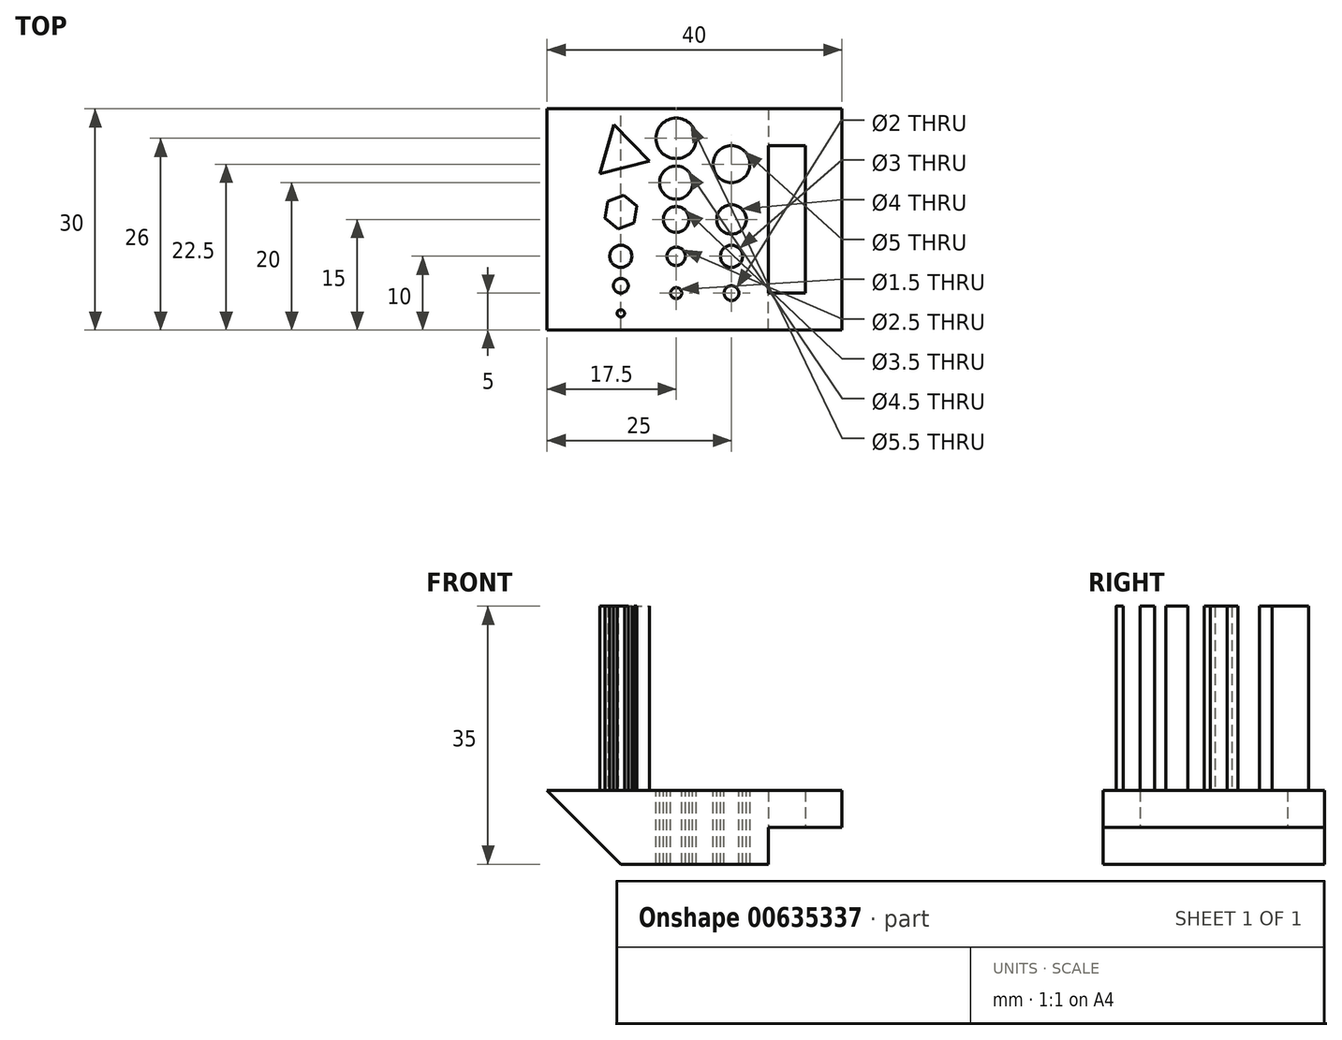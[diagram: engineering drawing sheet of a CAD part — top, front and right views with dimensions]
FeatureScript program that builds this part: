
annotation { "Feature Type Name" : "Feature", "Feature Type Description" : "" }
export const myFeature = defineFeature(function(context is Context, id is Id, definition is map)
    precondition{}
    {
        {
            var Q0;
            Q0=qCreatedBy(makeId("Top.planeOp"),FACE);
            var sketch = newSketch(context, id + "F0", { "sketchPlane" : qUnion([Q0])});
            skLineSegment(sketch, "E0.bottom", {"start": v(0, 0) * mm, "end": v(30, 0) * mm});
            skLineSegment(sketch, "E0.top", {"start": v(0, 30) * mm, "end": v(30, 30) * mm});
            skLineSegment(sketch, "E0.left", {"start": v(0, 0) * mm, "end": v(0, 30) * mm});
            skLineSegment(sketch, "E0.right", {"start": v(30, 0) * mm, "end": v(30, 30) * mm});
            skSolve(sketch);
        }
        {
            var Q0;
            Q0=makeQuery(id+"F0.imprint","IMPRINT",FACE,{"disambiguationData":[TD([[makeQuery(id+"F0.imprint","IMPRINT",EDGE,{"derivedFrom":sQuery(id+"F0.wireOp",EDGE,"E0.bottom")}),1.0]])]});
            extrude(context, id + "F1", {"entities" : qUnion([Q0]), "depth" : 10 * mm, "offsetDistance" : 25 * mm});
        }
        {
            var Q0;
            Q0=makeQuery(id+"F1.opExtrude","CAP_FACE",FACE,{"disambiguationData":[OSD([sQuery(id+"F0.wireOp",EDGE,"E0.bottom"),sQuery(id+"F0.wireOp",EDGE,"E0.top"),sQuery(id+"F0.wireOp",EDGE,"E0.left"),sQuery(id+"F0.wireOp",EDGE,"E0.right")])],"isStart":false});
            var sketch = newSketch(context, id + "F2", { "sketchPlane" : qUnion([Q0])});
            skLineSegment(sketch, "E1.bottom", {"start": v(0, 0) * mm, "end": v(10, 0) * mm});
            skLineSegment(sketch, "E1.top", {"start": v(0, 30) * mm, "end": v(10, 30) * mm});
            skLineSegment(sketch, "E1.left", {"start": v(0, 0) * mm, "end": v(0, 30) * mm});
            skLineSegment(sketch, "E1.right", {"start": v(10, 0) * mm, "end": v(10, 30) * mm});
            skSolve(sketch);
        }
        {
            var Q0;
            Q0=makeQuery(id+"F2.imprint","IMPRINT",FACE,{"disambiguationData":[TD([[makeQuery(id+"F2.imprint","IMPRINT",EDGE,{"derivedFrom":sQuery(id+"F2.wireOp",EDGE,"E1.bottom")}),1.0]])]});
            extrude(context, id + "F3", {"entities" : qUnion([Q0]), "operationType" : NewBodyOperationType.ADD, "depth" : 20 * mm, "offsetDistance" : 25 * mm});
        }
        {
            var Q0;
            Q0=makeQuery(id+"F1.opExtrude","CAP_FACE",FACE,{"disambiguationData":[OSD([sQuery(id+"F0.wireOp",EDGE,"E0.bottom"),sQuery(id+"F0.wireOp",EDGE,"E0.top"),sQuery(id+"F0.wireOp",EDGE,"E0.left"),sQuery(id+"F0.wireOp",EDGE,"E0.right")])],"isStart":false});
            var sketch = newSketch(context, id + "F4", { "sketchPlane" : qUnion([Q0])});
            skPoint(sketch, "E2", {"position": v(25, 5) * mm});
            skSolve(sketch);
        }
        {
            var Q0;
            Q0=sQuery(id+"F4.wireOp",VERTEX,"E2");
            var Q1;
            Q1=makeQuery(id+"F1.opExtrude","SWEPT_BODY",BODY,{"disambiguationData":[OSD([sQuery(id+"F0.wireOp",EDGE,"E0.bottom"),sQuery(id+"F0.wireOp",EDGE,"E0.top"),sQuery(id+"F0.wireOp",EDGE,"E0.left"),sQuery(id+"F0.wireOp",EDGE,"E0.right")])]});
            hole(context, id + "F5", {"style" : HoleStyle.SIMPLE, "endStyle" : HoleEndStyle.BLIND, "holeDiameter" : 2 * mm, "majorDiameter" : 5 * mm, "holeDepth" : 20 * mm, "isTappedThrough" : true, "tappedDepth" : 12 * mm, "tapClearance" : 3, "startFromSketch" : true, "locations" : qUnion([Q0]), "scope" : qUnion([Q1])});
        }
        {
            var Q0;
            Q0=makeQuery(id+"F1.opExtrude","CAP_FACE",FACE,{"disambiguationData":[OSD([sQuery(id+"F0.wireOp",EDGE,"E0.bottom"),sQuery(id+"F0.wireOp",EDGE,"E0.top"),sQuery(id+"F0.wireOp",EDGE,"E0.left"),sQuery(id+"F0.wireOp",EDGE,"E0.right")])],"isStart":false});
            var sketch = newSketch(context, id + "F6", { "sketchPlane" : qUnion([Q0])});
            skPoint(sketch, "E3", {"position": v(25, 10) * mm});
            skSolve(sketch);
        }
        {
            var Q0;
            Q0=sQuery(id+"F6.wireOp",VERTEX,"E3");
            var Q1;
            Q1=makeQuery(id+"F1.opExtrude","SWEPT_BODY",BODY,{"disambiguationData":[OSD([sQuery(id+"F0.wireOp",EDGE,"E0.bottom"),sQuery(id+"F0.wireOp",EDGE,"E0.top"),sQuery(id+"F0.wireOp",EDGE,"E0.left"),sQuery(id+"F0.wireOp",EDGE,"E0.right")])]});
            hole(context, id + "F7", {"style" : HoleStyle.SIMPLE, "endStyle" : HoleEndStyle.BLIND, "holeDiameter" : 3 * mm, "majorDiameter" : 5 * mm, "holeDepth" : 20 * mm, "isTappedThrough" : true, "tappedDepth" : 12 * mm, "tapClearance" : 3, "startFromSketch" : true, "locations" : qUnion([Q0]), "scope" : qUnion([Q1])});
        }
        {
            var Q0;
            Q0=makeQuery(id+"F1.opExtrude","CAP_FACE",FACE,{"disambiguationData":[OSD([sQuery(id+"F0.wireOp",EDGE,"E0.bottom"),sQuery(id+"F0.wireOp",EDGE,"E0.top"),sQuery(id+"F0.wireOp",EDGE,"E0.left"),sQuery(id+"F0.wireOp",EDGE,"E0.right")])],"isStart":false});
            var sketch = newSketch(context, id + "F8", { "sketchPlane" : qUnion([Q0])});
            skPoint(sketch, "E4", {"position": v(25, 15) * mm});
            skSolve(sketch);
        }
        {
            var Q0;
            Q0=sQuery(id+"F8.wireOp",VERTEX,"E4");
            var Q1;
            Q1=makeQuery(id+"F1.opExtrude","SWEPT_BODY",BODY,{"disambiguationData":[OSD([sQuery(id+"F0.wireOp",EDGE,"E0.bottom"),sQuery(id+"F0.wireOp",EDGE,"E0.top"),sQuery(id+"F0.wireOp",EDGE,"E0.left"),sQuery(id+"F0.wireOp",EDGE,"E0.right")])]});
            hole(context, id + "F9", {"style" : HoleStyle.SIMPLE, "endStyle" : HoleEndStyle.BLIND, "holeDiameter" : 4 * mm, "majorDiameter" : 5 * mm, "holeDepth" : 20 * mm, "isTappedThrough" : true, "tappedDepth" : 12 * mm, "tapClearance" : 3, "startFromSketch" : true, "locations" : qUnion([Q0]), "scope" : qUnion([Q1])});
        }
        {
            var Q0;
            Q0=makeQuery(id+"F1.opExtrude","CAP_FACE",FACE,{"disambiguationData":[OSD([sQuery(id+"F0.wireOp",EDGE,"E0.bottom"),sQuery(id+"F0.wireOp",EDGE,"E0.top"),sQuery(id+"F0.wireOp",EDGE,"E0.left"),sQuery(id+"F0.wireOp",EDGE,"E0.right")])],"isStart":false});
            var sketch = newSketch(context, id + "F10", { "sketchPlane" : qUnion([Q0])});
            skPoint(sketch, "E5", {"position": v(25, 22.5) * mm});
            skSolve(sketch);
        }
        {
            var Q0;
            Q0=sQuery(id+"F10.wireOp",VERTEX,"E5");
            var Q1;
            Q1=makeQuery(id+"F1.opExtrude","SWEPT_BODY",BODY,{"disambiguationData":[OSD([sQuery(id+"F0.wireOp",EDGE,"E0.bottom"),sQuery(id+"F0.wireOp",EDGE,"E0.top"),sQuery(id+"F0.wireOp",EDGE,"E0.left"),sQuery(id+"F0.wireOp",EDGE,"E0.right")])]});
            hole(context, id + "F11", {"style" : HoleStyle.SIMPLE, "endStyle" : HoleEndStyle.BLIND, "holeDiameter" : 5 * mm, "majorDiameter" : 5 * mm, "holeDepth" : 20 * mm, "isTappedThrough" : true, "tappedDepth" : 12 * mm, "tapClearance" : 3, "startFromSketch" : true, "locations" : qUnion([Q0]), "scope" : qUnion([Q1])});
        }
        {
            var Q0;
            Q0=makeQuery(id+"F1.opExtrude","CAP_FACE",FACE,{"disambiguationData":[OSD([sQuery(id+"F0.wireOp",EDGE,"E0.bottom"),sQuery(id+"F0.wireOp",EDGE,"E0.top"),sQuery(id+"F0.wireOp",EDGE,"E0.left"),sQuery(id+"F0.wireOp",EDGE,"E0.right")])],"isStart":false});
            var sketch = newSketch(context, id + "F12", { "sketchPlane" : qUnion([Q0])});
            skPoint(sketch, "E6", {"position": v(17.5, 5) * mm});
            skSolve(sketch);
        }
        {
            var Q0;
            Q0=sQuery(id+"F12.wireOp",VERTEX,"E6");
            var Q1;
            Q1=makeQuery(id+"F1.opExtrude","SWEPT_BODY",BODY,{"disambiguationData":[OSD([sQuery(id+"F0.wireOp",EDGE,"E0.bottom"),sQuery(id+"F0.wireOp",EDGE,"E0.top"),sQuery(id+"F0.wireOp",EDGE,"E0.left"),sQuery(id+"F0.wireOp",EDGE,"E0.right")])]});
            hole(context, id + "F13", {"style" : HoleStyle.SIMPLE, "endStyle" : HoleEndStyle.BLIND, "holeDiameter" : 1.5 * mm, "majorDiameter" : 5 * mm, "holeDepth" : 20 * mm, "isTappedThrough" : true, "tappedDepth" : 12 * mm, "tapClearance" : 3, "startFromSketch" : true, "locations" : qUnion([Q0]), "scope" : qUnion([Q1])});
        }
        {
            var Q0;
            Q0=makeQuery(id+"F1.opExtrude","CAP_FACE",FACE,{"disambiguationData":[OSD([sQuery(id+"F0.wireOp",EDGE,"E0.bottom"),sQuery(id+"F0.wireOp",EDGE,"E0.top"),sQuery(id+"F0.wireOp",EDGE,"E0.left"),sQuery(id+"F0.wireOp",EDGE,"E0.right")])],"isStart":false});
            var sketch = newSketch(context, id + "F14", { "sketchPlane" : qUnion([Q0])});
            skPoint(sketch, "E7", {"position": v(17.5, 10) * mm});
            skSolve(sketch);
        }
        {
            var Q0;
            Q0=sQuery(id+"F14.wireOp",VERTEX,"E7");
            var Q1;
            Q1=makeQuery(id+"F1.opExtrude","SWEPT_BODY",BODY,{"disambiguationData":[OSD([sQuery(id+"F0.wireOp",EDGE,"E0.bottom"),sQuery(id+"F0.wireOp",EDGE,"E0.top"),sQuery(id+"F0.wireOp",EDGE,"E0.left"),sQuery(id+"F0.wireOp",EDGE,"E0.right")])]});
            hole(context, id + "F15", {"style" : HoleStyle.SIMPLE, "endStyle" : HoleEndStyle.BLIND, "holeDiameter" : 2.5 * mm, "majorDiameter" : 5 * mm, "holeDepth" : 20 * mm, "isTappedThrough" : true, "tappedDepth" : 12 * mm, "tapClearance" : 3, "startFromSketch" : true, "locations" : qUnion([Q0]), "scope" : qUnion([Q1])});
        }
        {
            var Q0;
            Q0=makeQuery(id+"F1.opExtrude","CAP_FACE",FACE,{"disambiguationData":[OSD([sQuery(id+"F0.wireOp",EDGE,"E0.bottom"),sQuery(id+"F0.wireOp",EDGE,"E0.top"),sQuery(id+"F0.wireOp",EDGE,"E0.left"),sQuery(id+"F0.wireOp",EDGE,"E0.right")])],"isStart":false});
            var sketch = newSketch(context, id + "F16", { "sketchPlane" : qUnion([Q0])});
            skPoint(sketch, "E8", {"position": v(17.5, 15) * mm});
            skSolve(sketch);
        }
        {
            var Q0;
            Q0=sQuery(id+"F16.wireOp",VERTEX,"E8");
            var Q1;
            Q1=makeQuery(id+"F1.opExtrude","SWEPT_BODY",BODY,{"disambiguationData":[OSD([sQuery(id+"F0.wireOp",EDGE,"E0.bottom"),sQuery(id+"F0.wireOp",EDGE,"E0.top"),sQuery(id+"F0.wireOp",EDGE,"E0.left"),sQuery(id+"F0.wireOp",EDGE,"E0.right")])]});
            hole(context, id + "F17", {"style" : HoleStyle.SIMPLE, "endStyle" : HoleEndStyle.BLIND, "holeDiameter" : 3.5 * mm, "majorDiameter" : 5 * mm, "holeDepth" : 20 * mm, "isTappedThrough" : true, "tappedDepth" : 12 * mm, "tapClearance" : 3, "startFromSketch" : true, "locations" : qUnion([Q0]), "scope" : qUnion([Q1])});
        }
        {
            var Q0;
            Q0=makeQuery(id+"F1.opExtrude","CAP_FACE",FACE,{"disambiguationData":[OSD([sQuery(id+"F0.wireOp",EDGE,"E0.bottom"),sQuery(id+"F0.wireOp",EDGE,"E0.top"),sQuery(id+"F0.wireOp",EDGE,"E0.left"),sQuery(id+"F0.wireOp",EDGE,"E0.right")])],"isStart":false});
            var sketch = newSketch(context, id + "F18", { "sketchPlane" : qUnion([Q0])});
            skPoint(sketch, "E9", {"position": v(17.5, 20) * mm});
            skSolve(sketch);
        }
        {
            var Q0;
            Q0=sQuery(id+"F18.wireOp",VERTEX,"E9");
            var Q1;
            Q1=makeQuery(id+"F1.opExtrude","SWEPT_BODY",BODY,{"disambiguationData":[OSD([sQuery(id+"F0.wireOp",EDGE,"E0.bottom"),sQuery(id+"F0.wireOp",EDGE,"E0.top"),sQuery(id+"F0.wireOp",EDGE,"E0.left"),sQuery(id+"F0.wireOp",EDGE,"E0.right")])]});
            hole(context, id + "F19", {"style" : HoleStyle.SIMPLE, "endStyle" : HoleEndStyle.BLIND, "holeDiameter" : 4.5 * mm, "majorDiameter" : 5 * mm, "holeDepth" : 20 * mm, "isTappedThrough" : true, "tappedDepth" : 12 * mm, "tapClearance" : 3, "startFromSketch" : true, "locations" : qUnion([Q0]), "scope" : qUnion([Q1])});
        }
        {
            var Q0;
            Q0=makeQuery(id+"F1.opExtrude","CAP_FACE",FACE,{"disambiguationData":[OSD([sQuery(id+"F0.wireOp",EDGE,"E0.bottom"),sQuery(id+"F0.wireOp",EDGE,"E0.top"),sQuery(id+"F0.wireOp",EDGE,"E0.left"),sQuery(id+"F0.wireOp",EDGE,"E0.right")])],"isStart":false});
            var sketch = newSketch(context, id + "F20", { "sketchPlane" : qUnion([Q0])});
            skPoint(sketch, "E10", {"position": v(17.5, 26) * mm});
            skSolve(sketch);
        }
        {
            var Q0;
            Q0=sQuery(id+"F20.wireOp",VERTEX,"E10");
            var Q1;
            Q1=makeQuery(id+"F1.opExtrude","SWEPT_BODY",BODY,{"disambiguationData":[OSD([sQuery(id+"F0.wireOp",EDGE,"E0.bottom"),sQuery(id+"F0.wireOp",EDGE,"E0.top"),sQuery(id+"F0.wireOp",EDGE,"E0.left"),sQuery(id+"F0.wireOp",EDGE,"E0.right")])]});
            hole(context, id + "F21", {"style" : HoleStyle.SIMPLE, "endStyle" : HoleEndStyle.BLIND, "holeDiameter" : 5.5 * mm, "majorDiameter" : 5 * mm, "holeDepth" : 20 * mm, "isTappedThrough" : true, "tappedDepth" : 12 * mm, "tapClearance" : 3, "startFromSketch" : true, "locations" : qUnion([Q0]), "scope" : qUnion([Q1])});
        }
        {
            var Q0;
            Q0=makeQuery(id+"F3.opExtrude","CAP_FACE",FACE,{"disambiguationData":[OSD([sQuery(id+"F2.wireOp",EDGE,"E1.bottom"),sQuery(id+"F2.wireOp",EDGE,"E1.top"),sQuery(id+"F2.wireOp",EDGE,"E1.left"),sQuery(id+"F2.wireOp",EDGE,"E1.right")])],"isStart":false});
            extrude(context, id + "F22", {"entities" : qUnion([Q0]), "operationType" : NewBodyOperationType.REMOVE, "oppositeDirection" : true, "depth" : 20 * mm, "offsetDistance" : 25 * mm});
        }
        {
            var Q0;
            Q0=makeQuery(id+"F1.opExtrude","CAP_EDGE",EDGE,{"disambiguationData":[OSD([sQuery(id+"F0.wireOp",EDGE,"E0.left")])],"isStart":true});
            chamfer(context, id + "F23", {"entities" : qUnion([Q0]), "width" : 10 * mm, "tangentPropagation" : true});
        }
        {
            var Q0;
            Q0=makeQuery(id+"F22.boolean.opBoolean","MERGE",FACE,{"derivedFrom":[makeQuery(id+"F1.opExtrude","CAP_FACE",FACE,{"disambiguationData":[OSD([sQuery(id+"F0.wireOp",EDGE,"E0.bottom"),sQuery(id+"F0.wireOp",EDGE,"E0.top"),sQuery(id+"F0.wireOp",EDGE,"E0.left"),sQuery(id+"F0.wireOp",EDGE,"E0.right")])],"isStart":false}),makeQuery(id+"F22.opExtrude","CAP_FACE",FACE,{"disambiguationData":[OSD([sQuery(id+"F2.wireOp",EDGE,"E1.bottom"),sQuery(id+"F2.wireOp",EDGE,"E1.top"),sQuery(id+"F2.wireOp",EDGE,"E1.left"),sQuery(id+"F2.wireOp",EDGE,"E1.right")])],"isStart":false})]});
            var sketch = newSketch(context, id + "F24", { "sketchPlane" : qUnion([Q0])});
            skCircle(sketch, "E11", {"center": v(10, 6) * mm, "radius": 1 * mm});
            skSolve(sketch);
        }
        {
            var Q0;
            Q0=makeQuery(id+"F24.imprint","IMPRINT",FACE,{"disambiguationData":[TD([[makeQuery(id+"F24.imprint","IMPRINT",EDGE,{"derivedFrom":sQuery(id+"F24.wireOp",EDGE,"E11")}),1.0]])]});
            extrude(context, id + "F25", {"entities" : qUnion([Q0]), "operationType" : NewBodyOperationType.ADD, "depth" : 25 * mm, "offsetDistance" : 25 * mm});
        }
        {
            var Q0;
            Q0=makeQuery(id+"F22.boolean.opBoolean","MERGE",FACE,{"derivedFrom":[makeQuery(id+"F1.opExtrude","CAP_FACE",FACE,{"disambiguationData":[OSD([sQuery(id+"F0.wireOp",EDGE,"E0.bottom"),sQuery(id+"F0.wireOp",EDGE,"E0.top"),sQuery(id+"F0.wireOp",EDGE,"E0.left"),sQuery(id+"F0.wireOp",EDGE,"E0.right")])],"isStart":false}),makeQuery(id+"F22.opExtrude","CAP_FACE",FACE,{"disambiguationData":[OSD([sQuery(id+"F2.wireOp",EDGE,"E1.bottom"),sQuery(id+"F2.wireOp",EDGE,"E1.top"),sQuery(id+"F2.wireOp",EDGE,"E1.left"),sQuery(id+"F2.wireOp",EDGE,"E1.right")])],"isStart":false})]});
            var sketch = newSketch(context, id + "F26", { "sketchPlane" : qUnion([Q0])});
            skCircle(sketch, "E12", {"center": v(10, 10) * mm, "radius": 1.5 * mm});
            skSolve(sketch);
        }
        {
            var Q0;
            Q0=makeQuery(id+"F26.imprint","IMPRINT",FACE,{"disambiguationData":[TD([[makeQuery(id+"F26.imprint","IMPRINT",EDGE,{"derivedFrom":sQuery(id+"F26.wireOp",EDGE,"E12")}),1.0]])]});
            extrude(context, id + "F27", {"entities" : qUnion([Q0]), "operationType" : NewBodyOperationType.ADD, "depth" : 25 * mm, "offsetDistance" : 25 * mm});
        }
        {
            var Q0;
            Q0=makeQuery(id+"F22.boolean.opBoolean","MERGE",FACE,{"derivedFrom":[makeQuery(id+"F1.opExtrude","CAP_FACE",FACE,{"disambiguationData":[OSD([sQuery(id+"F0.wireOp",EDGE,"E0.bottom"),sQuery(id+"F0.wireOp",EDGE,"E0.top"),sQuery(id+"F0.wireOp",EDGE,"E0.left"),sQuery(id+"F0.wireOp",EDGE,"E0.right")])],"isStart":false}),makeQuery(id+"F22.opExtrude","CAP_FACE",FACE,{"disambiguationData":[OSD([sQuery(id+"F2.wireOp",EDGE,"E1.bottom"),sQuery(id+"F2.wireOp",EDGE,"E1.top"),sQuery(id+"F2.wireOp",EDGE,"E1.left"),sQuery(id+"F2.wireOp",EDGE,"E1.right")])],"isStart":false})]});
            var sketch = newSketch(context, id + "F28", { "sketchPlane" : qUnion([Q0])});
            skCircle(sketch, "E13", {"center": v(10, 2.25) * mm, "radius": 0.5 * mm});
            skSolve(sketch);
        }
        {
            var Q0;
            Q0=makeQuery(id+"F28.imprint","IMPRINT",FACE,{"disambiguationData":[TD([[makeQuery(id+"F28.imprint","IMPRINT",EDGE,{"derivedFrom":sQuery(id+"F28.wireOp",EDGE,"E13")}),1.0]])]});
            extrude(context, id + "F29", {"entities" : qUnion([Q0]), "operationType" : NewBodyOperationType.ADD, "depth" : 25 * mm, "offsetDistance" : 25 * mm});
        }
        {
            var Q0;
            Q0=makeQuery(id+"F22.boolean.opBoolean","MERGE",FACE,{"derivedFrom":[makeQuery(id+"F1.opExtrude","CAP_FACE",FACE,{"disambiguationData":[OSD([sQuery(id+"F0.wireOp",EDGE,"E0.bottom"),sQuery(id+"F0.wireOp",EDGE,"E0.top"),sQuery(id+"F0.wireOp",EDGE,"E0.left"),sQuery(id+"F0.wireOp",EDGE,"E0.right")])],"isStart":false}),makeQuery(id+"F22.opExtrude","CAP_FACE",FACE,{"disambiguationData":[OSD([sQuery(id+"F2.wireOp",EDGE,"E1.bottom"),sQuery(id+"F2.wireOp",EDGE,"E1.top"),sQuery(id+"F2.wireOp",EDGE,"E1.left"),sQuery(id+"F2.wireOp",EDGE,"E1.right")])],"isStart":false})]});
            var sketch = newSketch(context, id + "F30", { "sketchPlane" : qUnion([Q0])});
            skCircle(sketch, "E14.cCircle", {"center": v(10, 16) * mm, "radius": 2 * mm, "construction": true});
            skLineSegment(sketch, "E14.0", {"start": v(10.36, 18.28) * mm, "end": v(12.16, 16.83) * mm});
            skLineSegment(sketch, "E14.1", {"start": v(12.16, 16.83) * mm, "end": v(11.8, 14.55) * mm});
            skLineSegment(sketch, "E14.2", {"start": v(11.8, 14.55) * mm, "end": v(9.64, 13.72) * mm});
            skLineSegment(sketch, "E14.3", {"start": v(9.64, 13.72) * mm, "end": v(7.84, 15.17) * mm});
            skLineSegment(sketch, "E14.4", {"start": v(7.84, 15.17) * mm, "end": v(8.2, 17.45) * mm});
            skLineSegment(sketch, "E14.5", {"start": v(8.2, 17.45) * mm, "end": v(10.36, 18.28) * mm});
            skPoint(sketch, "E14.0.midPoint", {"position": v(11.26, 17.55) * mm});
            skSolve(sketch);
        }
        {
            var Q0;
            Q0=makeQuery(id+"F30.imprint","IMPRINT",FACE,{"disambiguationData":[TD([[makeQuery(id+"F30.imprint","IMPRINT",EDGE,{"derivedFrom":sQuery(id+"F30.wireOp",EDGE,"E14.0")}),-1.0]])]});
            extrude(context, id + "F31", {"entities" : qUnion([Q0]), "operationType" : NewBodyOperationType.ADD, "depth" : 25 * mm, "offsetDistance" : 25 * mm});
        }
        {
            var Q0;
            Q0=makeQuery(id+"F22.boolean.opBoolean","MERGE",FACE,{"derivedFrom":[makeQuery(id+"F1.opExtrude","CAP_FACE",FACE,{"disambiguationData":[OSD([sQuery(id+"F0.wireOp",EDGE,"E0.bottom"),sQuery(id+"F0.wireOp",EDGE,"E0.top"),sQuery(id+"F0.wireOp",EDGE,"E0.left"),sQuery(id+"F0.wireOp",EDGE,"E0.right")])],"isStart":false}),makeQuery(id+"F22.opExtrude","CAP_FACE",FACE,{"disambiguationData":[OSD([sQuery(id+"F2.wireOp",EDGE,"E1.bottom"),sQuery(id+"F2.wireOp",EDGE,"E1.top"),sQuery(id+"F2.wireOp",EDGE,"E1.left"),sQuery(id+"F2.wireOp",EDGE,"E1.right")])],"isStart":false})]});
            var sketch = newSketch(context, id + "F32", { "sketchPlane" : qUnion([Q0])});
            skCircle(sketch, "E15.cCircle", {"center": v(10, 24) * mm, "radius": 2 * mm, "construction": true});
            skLineSegment(sketch, "E15.0", {"start": v(9.03, 27.88) * mm, "end": v(13.85, 22.9) * mm});
            skLineSegment(sketch, "E15.1", {"start": v(13.85, 22.9) * mm, "end": v(7.12, 21.22) * mm});
            skLineSegment(sketch, "E15.2", {"start": v(7.12, 21.22) * mm, "end": v(9.03, 27.88) * mm});
            skPoint(sketch, "E15.0.midPoint", {"position": v(11.44, 25.39) * mm});
            skSolve(sketch);
        }
        {
            var Q0;
            Q0=makeQuery(id+"F32.imprint","IMPRINT",FACE,{"disambiguationData":[TD([[makeQuery(id+"F32.imprint","IMPRINT",EDGE,{"derivedFrom":sQuery(id+"F32.wireOp",EDGE,"E15.0")}),-1.0]])]});
            extrude(context, id + "F33", {"entities" : qUnion([Q0]), "operationType" : NewBodyOperationType.ADD, "depth" : 25 * mm, "offsetDistance" : 25 * mm});
        }
        {
            var Q0;
            Q0=makeQuery(id+"F1.opExtrude","SWEPT_FACE",FACE,{"disambiguationData":[OSD([sQuery(id+"F0.wireOp",EDGE,"E0.right")])]});
            var sketch = newSketch(context, id + "F34", { "sketchPlane" : qUnion([Q0])});
            skLineSegment(sketch, "E16.bottom", {"start": v(0, 10) * mm, "end": v(5, 10) * mm});
            skLineSegment(sketch, "E16.top", {"start": v(0, 5) * mm, "end": v(5, 5) * mm});
            skLineSegment(sketch, "E16.left", {"start": v(0, 10) * mm, "end": v(0, 5) * mm});
            skLineSegment(sketch, "E16.right", {"start": v(5, 10) * mm, "end": v(5, 5) * mm});
            skLineSegment(sketch, "E17.bottom", {"start": v(30, 10) * mm, "end": v(25, 10) * mm});
            skLineSegment(sketch, "E17.top", {"start": v(30, 5) * mm, "end": v(25, 5) * mm});
            skLineSegment(sketch, "E17.left", {"start": v(30, 10) * mm, "end": v(30, 5) * mm});
            skLineSegment(sketch, "E17.right", {"start": v(25, 10) * mm, "end": v(25, 5) * mm});
            skSolve(sketch);
        }
        {
            var Q0;
            Q0=makeQuery(id+"F34.imprint","IMPRINT",FACE,{"disambiguationData":[TD([[makeQuery(id+"F34.imprint","IMPRINT",EDGE,{"derivedFrom":sQuery(id+"F34.wireOp",EDGE,"E16.bottom")}),-1.0]])]});
            var Q1;
            Q1=makeQuery(id+"F34.imprint","IMPRINT",FACE,{"disambiguationData":[TD([[makeQuery(id+"F34.imprint","IMPRINT",EDGE,{"derivedFrom":sQuery(id+"F34.wireOp",EDGE,"E17.bottom")}),-1.0]])]});
            extrude(context, id + "F35", {"entities" : qUnion([Q0, Q1]), "operationType" : NewBodyOperationType.ADD, "depth" : 10 * mm, "offsetDistance" : 25 * mm});
        }
        {
            var Q0;
            Q0=makeQuery(id+"F35.opExtrude","SWEPT_FACE",FACE,{"disambiguationData":[OSD([sQuery(id+"F34.wireOp",EDGE,"E17.right")])]});
            var sketch = newSketch(context, id + "F36", { "sketchPlane" : qUnion([Q0])});
            skLineSegment(sketch, "E18.bottom", {"start": v(40, 10) * mm, "end": v(35, 10) * mm});
            skLineSegment(sketch, "E18.top", {"start": v(40, 5) * mm, "end": v(35, 5) * mm});
            skLineSegment(sketch, "E18.left", {"start": v(40, 10) * mm, "end": v(40, 5) * mm});
            skLineSegment(sketch, "E18.right", {"start": v(35, 10) * mm, "end": v(35, 5) * mm});
            skSolve(sketch);
        }
        {
            var Q0;
            Q0=makeQuery(id+"F36.imprint","IMPRINT",FACE,{"disambiguationData":[TD([[makeQuery(id+"F36.imprint","IMPRINT",EDGE,{"derivedFrom":sQuery(id+"F36.wireOp",EDGE,"E18.bottom")}),1.0]])]});
            extrude(context, id + "F37", {"entities" : qUnion([Q0]), "operationType" : NewBodyOperationType.ADD, "depth" : 25 * mm, "offsetDistance" : 25 * mm});
        }
    });
